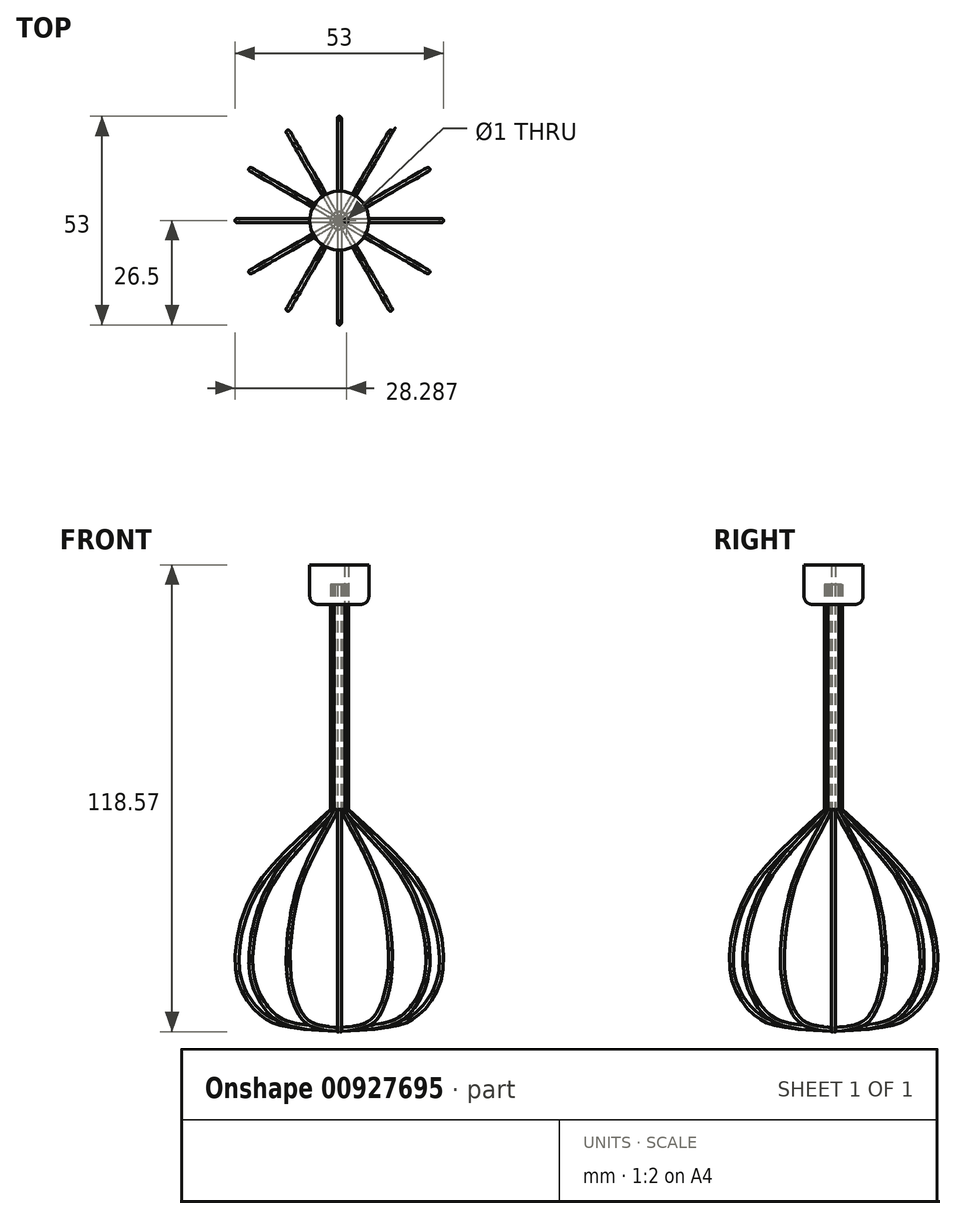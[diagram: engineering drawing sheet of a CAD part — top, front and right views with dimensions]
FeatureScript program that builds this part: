
annotation { "Feature Type Name" : "Feature", "Feature Type Description" : "" }
export const myFeature = defineFeature(function(context is Context, id is Id, definition is map)
    precondition{}
    {
        {
            var Q0;
            Q0=qCreatedBy(makeId("Front.planeOp"),FACE);
            var sketch = newSketch(context, id + "F0", { "sketchPlane" : qUnion([Q0])});
            skLineSegment(sketch, "E0", {"start": v(17.9, 90) * mm, "end": v(17.9, 39.8) * mm});
            skFitSpline(sketch, "E1", {"points": [v(17.9, 39.8) * mm, v(35.7, 19.25) * mm, v(41.63, -11.33) * mm, v(31.13, -30.5) * mm, v(17.9, -37.34) * mm, v(0, -39.17) * mm], "startDerivative": vector(89.54, -81.96) * mm, "endDerivative": vector(-103.82, -4.35) * mm});
            skLineSegment(sketch, "E2", {"start": v(0, 99.4) * mm, "end": v(0, -50.63) * mm});
            skSolve(sketch);
        }
        {
            var Q0;
            Q0=qCreatedBy(makeId("Top.planeOp"),FACE);
            cPlane(context, id + "F1", {"entities" : qUnion([Q0]), "cplaneType" : CPlaneType.OFFSET, "offset" : 90 * mm, "width" : 150 * mm, "height" : 150 * mm});
        }
        {
            var Q0;
            Q0=qCreatedBy(id+"F1.planeOp",FACE);
            var sketch = newSketch(context, id + "F2", { "sketchPlane" : qUnion([Q0])});
            skCircle(sketch, "E3", {"center": v(1.79, 0) * mm, "radius": 0.5 * mm});
            skCircle(sketch, "E4", {"center": v(0, 0) * mm, "radius": 7.5 * mm});
            skSolve(sketch);
        }
        {
            var Q0;
            Q0=makeQuery(id+"F2.imprint","IMPRINT",FACE,{"disambiguationData":[TD([[makeQuery(id+"F2.imprint","IMPRINT",EDGE,{"derivedFrom":sQuery(id+"F2.wireOp",EDGE,"E3")}),1.0]])]});
            var Q1;
            Q1=sQuery(id+"F0.wireOp",EDGE,"E0");
            var Q2;
            Q2=sQuery(id+"F0.wireOp",EDGE,"E1");
            sweep(context, id + "F3", {"profiles" : qUnion([Q0]), "path" : qUnion([Q1, Q2])});
        }
        {
            var Q0;
            Q0=makeQuery(id+"F3.opSweep","SWEPT_BODY",BODY,{"disambiguationData":[OSD([sQuery(id+"F0.wireOp",EDGE,"E1"),sQuery(id+"F2.wireOp",EDGE,"E3")])]});
            var Q1;
            Q1=sQuery(id+"F0.wireOp",EDGE,"E2");
            circularPattern(context, id + "F4", {"entities" : qUnion([Q0]), "axis" : qUnion([Q1]), "angle" : 360 * degree, "instanceCount" : 12, "equalSpace" : true});
        }
        {
            var Q0;
            Q0=makeQuery(id+"F2.imprint","IMPRINT",FACE,{"disambiguationData":[TD([[makeQuery(id+"F2.imprint","IMPRINT",EDGE,{"derivedFrom":sQuery(id+"F2.wireOp",EDGE,"E3")}),-1.0]])]});
            extrude(context, id + "F5", {"entities" : qUnion([Q0]), "endBound" : BoundingType.SYMMETRIC, "depth" : 10 * mm, "offsetDistance" : 25 * mm});
        }
        {
            var Q0;
            Q0=makeQuery(id+"F5.opExtrude","CAP_EDGE",EDGE,{"disambiguationData":[OSD([sQuery(id+"F2.wireOp",EDGE,"E4")])],"isStart":true});
            fillet(context, id + "F6", {"entities" : qUnion([Q0]), "radius" : 2 * mm, "tangentPropagation" : true, "allowEdgeOverflow" : false});
        }
        {
            var Q0;
            Q0=makeQuery(id+"F3.opSweep","SWEPT_BODY",BODY,{"disambiguationData":[OSD([sQuery(id+"F0.wireOp",EDGE,"E1"),sQuery(id+"F2.wireOp",EDGE,"E3")])]});
            var Q1;
            Q1=makeQuery(id+"F4.opPattern","COPY",BODY,{"derivedFrom":makeQuery(id+"F3.opSweep","SWEPT_BODY",BODY,{"disambiguationData":[OSD([sQuery(id+"F0.wireOp",EDGE,"E1"),sQuery(id+"F2.wireOp",EDGE,"E3")])]}),"instanceName":"11"});
            var Q2;
            Q2=makeQuery(id+"F4.opPattern","COPY",BODY,{"derivedFrom":makeQuery(id+"F3.opSweep","SWEPT_BODY",BODY,{"disambiguationData":[OSD([sQuery(id+"F0.wireOp",EDGE,"E1"),sQuery(id+"F2.wireOp",EDGE,"E3")])]}),"instanceName":"1"});
            var Q3;
            Q3=makeQuery(id+"F4.opPattern","COPY",BODY,{"derivedFrom":makeQuery(id+"F3.opSweep","SWEPT_BODY",BODY,{"disambiguationData":[OSD([sQuery(id+"F0.wireOp",EDGE,"E1"),sQuery(id+"F2.wireOp",EDGE,"E3")])]}),"instanceName":"3"});
            var Q4;
            Q4=makeQuery(id+"F4.opPattern","COPY",BODY,{"derivedFrom":makeQuery(id+"F3.opSweep","SWEPT_BODY",BODY,{"disambiguationData":[OSD([sQuery(id+"F0.wireOp",EDGE,"E1"),sQuery(id+"F2.wireOp",EDGE,"E3")])]}),"instanceName":"2"});
            var Q5;
            Q5=makeQuery(id+"F4.opPattern","COPY",BODY,{"derivedFrom":makeQuery(id+"F3.opSweep","SWEPT_BODY",BODY,{"disambiguationData":[OSD([sQuery(id+"F0.wireOp",EDGE,"E1"),sQuery(id+"F2.wireOp",EDGE,"E3")])]}),"instanceName":"4"});
            var Q6;
            Q6=makeQuery(id+"F4.opPattern","COPY",BODY,{"derivedFrom":makeQuery(id+"F3.opSweep","SWEPT_BODY",BODY,{"disambiguationData":[OSD([sQuery(id+"F0.wireOp",EDGE,"E1"),sQuery(id+"F2.wireOp",EDGE,"E3")])]}),"instanceName":"5"});
            var Q7;
            Q7=makeQuery(id+"F4.opPattern","COPY",BODY,{"derivedFrom":makeQuery(id+"F3.opSweep","SWEPT_BODY",BODY,{"disambiguationData":[OSD([sQuery(id+"F0.wireOp",EDGE,"E1"),sQuery(id+"F2.wireOp",EDGE,"E3")])]}),"instanceName":"6"});
            var Q8;
            Q8=makeQuery(id+"F4.opPattern","COPY",BODY,{"derivedFrom":makeQuery(id+"F3.opSweep","SWEPT_BODY",BODY,{"disambiguationData":[OSD([sQuery(id+"F0.wireOp",EDGE,"E1"),sQuery(id+"F2.wireOp",EDGE,"E3")])]}),"instanceName":"7"});
            var Q9;
            Q9=makeQuery(id+"F4.opPattern","COPY",BODY,{"derivedFrom":makeQuery(id+"F3.opSweep","SWEPT_BODY",BODY,{"disambiguationData":[OSD([sQuery(id+"F0.wireOp",EDGE,"E1"),sQuery(id+"F2.wireOp",EDGE,"E3")])]}),"instanceName":"8"});
            var Q10;
            Q10=makeQuery(id+"F4.opPattern","COPY",BODY,{"derivedFrom":makeQuery(id+"F3.opSweep","SWEPT_BODY",BODY,{"disambiguationData":[OSD([sQuery(id+"F0.wireOp",EDGE,"E1"),sQuery(id+"F2.wireOp",EDGE,"E3")])]}),"instanceName":"9"});
            var Q11;
            Q11=makeQuery(id+"F4.opPattern","COPY",BODY,{"derivedFrom":makeQuery(id+"F3.opSweep","SWEPT_BODY",BODY,{"disambiguationData":[OSD([sQuery(id+"F0.wireOp",EDGE,"E1"),sQuery(id+"F2.wireOp",EDGE,"E3")])]}),"instanceName":"10"});
            transform(context, id + "F7", {"entities" : qUnion([Q0, Q1, Q2, Q3, Q4, Q5, Q6, Q7, Q8, Q9, Q10, Q11]), "transformType" : TransformType.TRANSLATION_3D, "dx" : 0 * mm, "dy" : 0 * mm, "dz" : 0 * mm, "makeCopy" : true});
        }
        {
            var Q0;
            Q0=makeQuery(id+"F7.opPattern","COPY",BODY,{"derivedFrom":makeQuery(id+"F3.opSweep","SWEPT_BODY",BODY,{"disambiguationData":[OSD([sQuery(id+"F0.wireOp",EDGE,"E1"),sQuery(id+"F2.wireOp",EDGE,"E3")])]}),"instanceName":"1"});
            var Q1;
            Q1=makeQuery(id+"F7.opPattern","COPY",BODY,{"derivedFrom":makeQuery(id+"F4.opPattern","COPY",BODY,{"derivedFrom":makeQuery(id+"F3.opSweep","SWEPT_BODY",BODY,{"disambiguationData":[OSD([sQuery(id+"F0.wireOp",EDGE,"E1"),sQuery(id+"F2.wireOp",EDGE,"E3")])]}),"instanceName":"1"}),"instanceName":"1"});
            var Q2;
            Q2=makeQuery(id+"F7.opPattern","COPY",BODY,{"derivedFrom":makeQuery(id+"F4.opPattern","COPY",BODY,{"derivedFrom":makeQuery(id+"F3.opSweep","SWEPT_BODY",BODY,{"disambiguationData":[OSD([sQuery(id+"F0.wireOp",EDGE,"E1"),sQuery(id+"F2.wireOp",EDGE,"E3")])]}),"instanceName":"2"}),"instanceName":"1"});
            var Q3;
            Q3=makeQuery(id+"F7.opPattern","COPY",BODY,{"derivedFrom":makeQuery(id+"F4.opPattern","COPY",BODY,{"derivedFrom":makeQuery(id+"F3.opSweep","SWEPT_BODY",BODY,{"disambiguationData":[OSD([sQuery(id+"F0.wireOp",EDGE,"E1"),sQuery(id+"F2.wireOp",EDGE,"E3")])]}),"instanceName":"3"}),"instanceName":"1"});
            var Q4;
            Q4=makeQuery(id+"F7.opPattern","COPY",BODY,{"derivedFrom":makeQuery(id+"F4.opPattern","COPY",BODY,{"derivedFrom":makeQuery(id+"F3.opSweep","SWEPT_BODY",BODY,{"disambiguationData":[OSD([sQuery(id+"F0.wireOp",EDGE,"E1"),sQuery(id+"F2.wireOp",EDGE,"E3")])]}),"instanceName":"4"}),"instanceName":"1"});
            var Q5;
            Q5=makeQuery(id+"F7.opPattern","COPY",BODY,{"derivedFrom":makeQuery(id+"F4.opPattern","COPY",BODY,{"derivedFrom":makeQuery(id+"F3.opSweep","SWEPT_BODY",BODY,{"disambiguationData":[OSD([sQuery(id+"F0.wireOp",EDGE,"E1"),sQuery(id+"F2.wireOp",EDGE,"E3")])]}),"instanceName":"5"}),"instanceName":"1"});
            var Q6;
            Q6=makeQuery(id+"F7.opPattern","COPY",BODY,{"derivedFrom":makeQuery(id+"F4.opPattern","COPY",BODY,{"derivedFrom":makeQuery(id+"F3.opSweep","SWEPT_BODY",BODY,{"disambiguationData":[OSD([sQuery(id+"F0.wireOp",EDGE,"E1"),sQuery(id+"F2.wireOp",EDGE,"E3")])]}),"instanceName":"6"}),"instanceName":"1"});
            var Q7;
            Q7=makeQuery(id+"F7.opPattern","COPY",BODY,{"derivedFrom":makeQuery(id+"F4.opPattern","COPY",BODY,{"derivedFrom":makeQuery(id+"F3.opSweep","SWEPT_BODY",BODY,{"disambiguationData":[OSD([sQuery(id+"F0.wireOp",EDGE,"E1"),sQuery(id+"F2.wireOp",EDGE,"E3")])]}),"instanceName":"7"}),"instanceName":"1"});
            var Q8;
            Q8=makeQuery(id+"F7.opPattern","COPY",BODY,{"derivedFrom":makeQuery(id+"F4.opPattern","COPY",BODY,{"derivedFrom":makeQuery(id+"F3.opSweep","SWEPT_BODY",BODY,{"disambiguationData":[OSD([sQuery(id+"F0.wireOp",EDGE,"E1"),sQuery(id+"F2.wireOp",EDGE,"E3")])]}),"instanceName":"8"}),"instanceName":"1"});
            var Q9;
            Q9=makeQuery(id+"F7.opPattern","COPY",BODY,{"derivedFrom":makeQuery(id+"F4.opPattern","COPY",BODY,{"derivedFrom":makeQuery(id+"F3.opSweep","SWEPT_BODY",BODY,{"disambiguationData":[OSD([sQuery(id+"F0.wireOp",EDGE,"E1"),sQuery(id+"F2.wireOp",EDGE,"E3")])]}),"instanceName":"9"}),"instanceName":"1"});
            var Q10;
            Q10=makeQuery(id+"F7.opPattern","COPY",BODY,{"derivedFrom":makeQuery(id+"F4.opPattern","COPY",BODY,{"derivedFrom":makeQuery(id+"F3.opSweep","SWEPT_BODY",BODY,{"disambiguationData":[OSD([sQuery(id+"F0.wireOp",EDGE,"E1"),sQuery(id+"F2.wireOp",EDGE,"E3")])]}),"instanceName":"10"}),"instanceName":"1"});
            var Q11;
            Q11=makeQuery(id+"F7.opPattern","COPY",BODY,{"derivedFrom":makeQuery(id+"F4.opPattern","COPY",BODY,{"derivedFrom":makeQuery(id+"F3.opSweep","SWEPT_BODY",BODY,{"disambiguationData":[OSD([sQuery(id+"F0.wireOp",EDGE,"E1"),sQuery(id+"F2.wireOp",EDGE,"E3")])]}),"instanceName":"11"}),"instanceName":"1"});
            var Q12;
            Q12=makeQuery(id+"F5.opExtrude","SWEPT_BODY",BODY,{"disambiguationData":[OSD([sQuery(id+"F2.wireOp",EDGE,"E3"),sQuery(id+"F2.wireOp",EDGE,"E4")])]});
            booleanBodies(context, id + "F8", {"operationType" : BooleanOperationType.SUBTRACTION, "tools" : qUnion([Q0, Q1, Q2, Q3, Q4, Q5, Q6, Q7, Q8, Q9, Q10, Q11]), "targets" : qUnion([Q12])});
        }
    });
